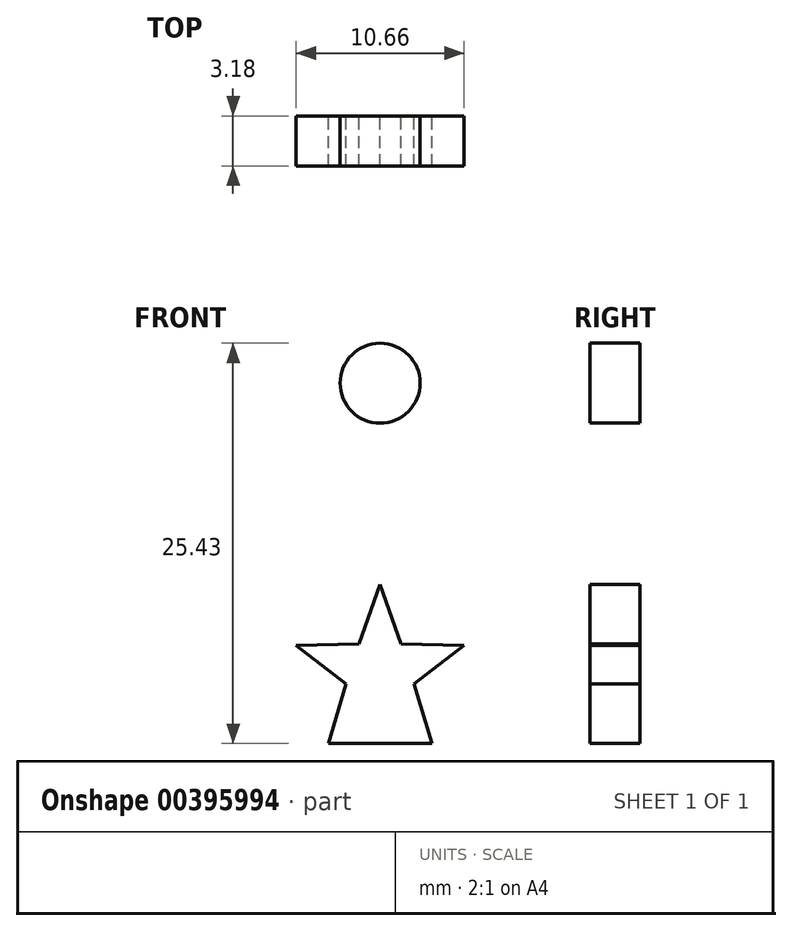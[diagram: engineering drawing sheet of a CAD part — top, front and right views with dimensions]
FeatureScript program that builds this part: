
annotation { "Feature Type Name" : "Feature", "Feature Type Description" : "" }
export const myFeature = defineFeature(function(context is Context, id is Id, definition is map)
    precondition{}
    {
        {
            var Q0;
            Q0=qCreatedBy(makeId("Front.planeOp"),FACE);
            var sketch = newSketch(context, id + "F0", { "sketchPlane" : qUnion([Q0])});
            skLineSegment(sketch, "E0", {"start": v(-0.1, 38.27) * mm, "end": v(-3.28, 38.27) * mm});
            skLineSegment(sketch, "E1", {"start": v(-3.28, 38.27) * mm, "end": v(-2.16, 42.06) * mm});
            skLineSegment(sketch, "E2", {"start": v(-2.16, 42.06) * mm, "end": v(-5.33, 44.5) * mm});
            skLineSegment(sketch, "E3", {"start": v(-5.33, 44.5) * mm, "end": v(-1.33, 44.6) * mm});
            skLineSegment(sketch, "E4", {"start": v(-1.33, 44.6) * mm, "end": v(0, 48.37) * mm});
            skLineSegment(sketch, "E5", {"start": v(0, 48.37) * mm, "end": v(1.33, 44.6) * mm});
            skLineSegment(sketch, "E6", {"start": v(1.33, 44.6) * mm, "end": v(5.33, 44.5) * mm});
            skLineSegment(sketch, "E7", {"start": v(5.33, 44.5) * mm, "end": v(2.16, 42.06) * mm});
            skLineSegment(sketch, "E8", {"start": v(2.16, 42.06) * mm, "end": v(3.28, 38.27) * mm});
            skLineSegment(sketch, "E9", {"start": v(3.28, 38.27) * mm, "end": v(-0.1, 38.27) * mm});
            skLineSegment(sketch, "E10", {"start": v(-31.05, -65.39) * mm, "end": v(-1.59, -65.39) * mm});
            skLineSegment(sketch, "E11", {"start": v(-1.59, -65.39) * mm, "end": v(-1.59, -0.36) * mm});
            skLineSegment(sketch, "E12", {"start": v(-1.59, -0.36) * mm, "end": v(1.59, -0.36) * mm});
            skLineSegment(sketch, "E13", {"start": v(1.59, -0.36) * mm, "end": v(1.59, -65.39) * mm});
            skLineSegment(sketch, "E14", {"start": v(1.59, -65.39) * mm, "end": v(31.05, -65.39) * mm});
            skLineSegment(sketch, "E15", {"start": v(31.05, -65.39) * mm, "end": v(31.05, -57.77) * mm});
            skLineSegment(sketch, "E16", {"start": v(31.05, -57.77) * mm, "end": v(27.9, -54.66) * mm});
            skLineSegment(sketch, "E17", {"start": v(23.62, -52.86) * mm, "end": v(21.6, -52.86) * mm});
            skLineSegment(sketch, "E18", {"start": v(9.72, -41.76) * mm, "end": v(8.89, -31.88) * mm});
            skLineSegment(sketch, "E19", {"start": v(23.02, -32.1) * mm, "end": v(23.54, -32.53) * mm});
            skLineSegment(sketch, "E20", {"start": v(23.54, -32.53) * mm, "end": v(29.79, -39.65) * mm});
            skLineSegment(sketch, "E21", {"start": v(29.79, -39.65) * mm, "end": v(30.65, -38.56) * mm});
            skLineSegment(sketch, "E22", {"start": v(30.65, -38.56) * mm, "end": v(24.6, -31.68) * mm});
            skLineSegment(sketch, "E23", {"start": v(24.6, -31.68) * mm, "end": v(26.15, -31.56) * mm});
            skLineSegment(sketch, "E24", {"start": v(36.9, -31.24) * mm, "end": v(41.54, -31.28) * mm});
            skLineSegment(sketch, "E25", {"start": v(42.55, -31.58) * mm, "end": v(42.82, -31.78) * mm});
            skLineSegment(sketch, "E26", {"start": v(42.82, -31.78) * mm, "end": v(45.54, -34.23) * mm});
            skLineSegment(sketch, "E27", {"start": v(45.54, -34.23) * mm, "end": v(46.28, -33.04) * mm});
            skLineSegment(sketch, "E28", {"start": v(46.28, -33.04) * mm, "end": v(44.43, -31.37) * mm});
            skLineSegment(sketch, "E29", {"start": v(44.43, -31.37) * mm, "end": v(48.37, -31.55) * mm});
            skLineSegment(sketch, "E30", {"start": v(48.37, -31.55) * mm, "end": v(48.44, -30.07) * mm});
            skLineSegment(sketch, "E31", {"start": v(48.44, -30.07) * mm, "end": v(42.79, -29.82) * mm});
            skLineSegment(sketch, "E32", {"start": v(42.79, -29.82) * mm, "end": v(45.23, -26.96) * mm});
            skLineSegment(sketch, "E33", {"start": v(45.23, -26.96) * mm, "end": v(44.36, -25.9) * mm});
            skLineSegment(sketch, "E34", {"start": v(44.36, -25.9) * mm, "end": v(41.7, -29.01) * mm});
            skLineSegment(sketch, "E35", {"start": v(40.75, -29.68) * mm, "end": v(40.18, -29.77) * mm});
            skLineSegment(sketch, "E36", {"start": v(40.18, -29.77) * mm, "end": v(38.93, -29.75) * mm});
            skLineSegment(sketch, "E37", {"start": v(28.15, -29.96) * mm, "end": v(36.05, -22.74) * mm});
            skLineSegment(sketch, "E38", {"start": v(36.05, -22.74) * mm, "end": v(35.3, -21.56) * mm});
            skLineSegment(sketch, "E39", {"start": v(35.3, -21.56) * mm, "end": v(26.43, -29.66) * mm});
            skLineSegment(sketch, "E40", {"start": v(26.08, -29.9) * mm, "end": v(25.34, -30.14) * mm});
            skLineSegment(sketch, "E41", {"start": v(16.62, -30.53) * mm, "end": v(12.38, -30.51) * mm});
            skLineSegment(sketch, "E42", {"start": v(12.38, -30.51) * mm, "end": v(15.43, -26.53) * mm});
            skLineSegment(sketch, "E43", {"start": v(15.43, -26.53) * mm, "end": v(14.51, -25.52) * mm});
            skLineSegment(sketch, "E44", {"start": v(14.51, -25.52) * mm, "end": v(11.37, -29.64) * mm});
            skLineSegment(sketch, "E45", {"start": v(10.48, -30.32) * mm, "end": v(9.87, -30.44) * mm});
            skLineSegment(sketch, "E46", {"start": v(9.87, -30.44) * mm, "end": v(8.76, -30.37) * mm});
            skLineSegment(sketch, "E47", {"start": v(8.76, -30.37) * mm, "end": v(6.95, -8.97) * mm});
            skLineSegment(sketch, "E48", {"start": v(6.95, -8.97) * mm, "end": v(18.25, -9.22) * mm});
            skLineSegment(sketch, "E49", {"start": v(18.25, -9.22) * mm, "end": v(24, -15.05) * mm});
            skLineSegment(sketch, "E50", {"start": v(24, -15.05) * mm, "end": v(24.8, -13.9) * mm});
            skLineSegment(sketch, "E51", {"start": v(24.8, -13.9) * mm, "end": v(20.18, -9.22) * mm});
            skLineSegment(sketch, "E52", {"start": v(20.18, -9.22) * mm, "end": v(31.03, -9.05) * mm});
            skLineSegment(sketch, "E53", {"start": v(32.03, -9.3) * mm, "end": v(32.45, -9.62) * mm});
            skLineSegment(sketch, "E54", {"start": v(32.45, -9.62) * mm, "end": v(34.33, -11.52) * mm});
            skLineSegment(sketch, "E55", {"start": v(34.33, -11.52) * mm, "end": v(35.13, -10.38) * mm});
            skLineSegment(sketch, "E56", {"start": v(35.13, -10.38) * mm, "end": v(33.72, -8.96) * mm});
            skLineSegment(sketch, "E57", {"start": v(33.72, -8.96) * mm, "end": v(36.34, -8.85) * mm});
            skLineSegment(sketch, "E58", {"start": v(36.34, -8.85) * mm, "end": v(36.3, -7.36) * mm});
            skLineSegment(sketch, "E59", {"start": v(36.3, -7.36) * mm, "end": v(32.78, -7.5) * mm});
            skLineSegment(sketch, "E60", {"start": v(32.78, -7.5) * mm, "end": v(34.25, -4.43) * mm});
            skLineSegment(sketch, "E61", {"start": v(34.25, -4.43) * mm, "end": v(33.17, -3.69) * mm});
            skLineSegment(sketch, "E62", {"start": v(33.17, -3.69) * mm, "end": v(31.91, -6.33) * mm});
            skLineSegment(sketch, "E63", {"start": v(15.62, -7.71) * mm, "end": v(12.56, -7.66) * mm});
            skLineSegment(sketch, "E64", {"start": v(12.56, -7.66) * mm, "end": v(21.21, 0.02) * mm});
            skLineSegment(sketch, "E65", {"start": v(21.21, 0.02) * mm, "end": v(20.47, 1.21) * mm});
            skLineSegment(sketch, "E66", {"start": v(20.47, 1.21) * mm, "end": v(11.1, -7.1) * mm});
            skLineSegment(sketch, "E67", {"start": v(9.81, -7.6) * mm, "end": v(6.83, -7.49) * mm});
            skLineSegment(sketch, "E68", {"start": v(6.83, -7.49) * mm, "end": v(5.27, 11) * mm});
            skLineSegment(sketch, "E69", {"start": v(5.27, 11) * mm, "end": v(7.7, 11.24) * mm});
            skLineSegment(sketch, "E70", {"start": v(9.44, 10.36) * mm, "end": v(9.58, 10.14) * mm});
            skLineSegment(sketch, "E71", {"start": v(9.58, 10.14) * mm, "end": v(12.8, 4.4) * mm});
            skLineSegment(sketch, "E72", {"start": v(12.8, 4.4) * mm, "end": v(13.83, 5.22) * mm});
            skLineSegment(sketch, "E73", {"start": v(13.83, 5.22) * mm, "end": v(10.35, 11.43) * mm});
            skLineSegment(sketch, "E74", {"start": v(23.44, 10.8) * mm, "end": v(23.9, 10.3) * mm});
            skLineSegment(sketch, "E75", {"start": v(23.9, 10.3) * mm, "end": v(25.93, 7.4) * mm});
            skLineSegment(sketch, "E76", {"start": v(25.93, 7.4) * mm, "end": v(26.88, 8.36) * mm});
            skLineSegment(sketch, "E77", {"start": v(26.88, 8.36) * mm, "end": v(24.89, 11.22) * mm});
            skLineSegment(sketch, "E78", {"start": v(24.53, 13.68) * mm, "end": v(24.67, 14.03) * mm});
            skLineSegment(sketch, "E79", {"start": v(24.67, 14.03) * mm, "end": v(25.54, 15.93) * mm});
            skLineSegment(sketch, "E80", {"start": v(25.54, 15.93) * mm, "end": v(24.46, 16.65) * mm});
            skLineSegment(sketch, "E81", {"start": v(24.46, 16.65) * mm, "end": v(23.26, 14.07) * mm});
            skLineSegment(sketch, "E82", {"start": v(21.6, 12.8) * mm, "end": v(21.3, 12.79) * mm});
            skLineSegment(sketch, "E83", {"start": v(21.3, 12.79) * mm, "end": v(20.17, 12.87) * mm});
            skLineSegment(sketch, "E84", {"start": v(13.2, 13.03) * mm, "end": v(15.15, 15.75) * mm});
            skLineSegment(sketch, "E85", {"start": v(15.15, 15.75) * mm, "end": v(14.2, 16.72) * mm});
            skLineSegment(sketch, "E86", {"start": v(14.2, 16.72) * mm, "end": v(12.12, 13.8) * mm});
            skLineSegment(sketch, "E87", {"start": v(11.24, 13.08) * mm, "end": v(10.63, 12.94) * mm});
            skLineSegment(sketch, "E88", {"start": v(10.63, 12.94) * mm, "end": v(5.14, 12.49) * mm});
            skLineSegment(sketch, "E89", {"start": v(5.14, 12.49) * mm, "end": v(4.12, 24.6) * mm});
            skLineSegment(sketch, "E90", {"start": v(4.12, 24.6) * mm, "end": v(8.75, 24.04) * mm});
            skLineSegment(sketch, "E91", {"start": v(9.7, 23.68) * mm, "end": v(9.9, 23.51) * mm});
            skLineSegment(sketch, "E92", {"start": v(9.9, 23.51) * mm, "end": v(13.41, 20.18) * mm});
            skLineSegment(sketch, "E93", {"start": v(13.41, 20.18) * mm, "end": v(14.18, 21.35) * mm});
            skLineSegment(sketch, "E94", {"start": v(14.18, 21.35) * mm, "end": v(11.35, 24.04) * mm});
            skLineSegment(sketch, "E95", {"start": v(19.16, 25.44) * mm, "end": v(18.84, 26.88) * mm});
            skLineSegment(sketch, "E96", {"start": v(18.84, 26.88) * mm, "end": v(16.38, 26.2) * mm});
            skLineSegment(sketch, "E97", {"start": v(16.38, 26.2) * mm, "end": v(17.83, 28.73) * mm});
            skLineSegment(sketch, "E98", {"start": v(17.83, 28.73) * mm, "end": v(16.81, 29.58) * mm});
            skLineSegment(sketch, "E99", {"start": v(16.81, 29.58) * mm, "end": v(15.2, 26.8) * mm});
            skLineSegment(sketch, "E100", {"start": v(9.54, 25.56) * mm, "end": v(11.07, 28.68) * mm});
            skLineSegment(sketch, "E101", {"start": v(11.07, 28.68) * mm, "end": v(10, 29.43) * mm});
            skLineSegment(sketch, "E102", {"start": v(10, 29.43) * mm, "end": v(8.77, 26.93) * mm});
            skLineSegment(sketch, "E103", {"start": v(7.07, 25.7) * mm, "end": v(6.76, 25.71) * mm});
            skLineSegment(sketch, "E104", {"start": v(6.76, 25.71) * mm, "end": v(4, 26.16) * mm});
            skLineSegment(sketch, "E105", {"start": v(4, 26.16) * mm, "end": v(3.23, 35.19) * mm});
            skLineSegment(sketch, "E106", {"start": v(3.23, 35.19) * mm, "end": v(7.77, 32.06) * mm});
            skLineSegment(sketch, "E107", {"start": v(7.77, 32.06) * mm, "end": v(5.09, 41.1) * mm});
            skLineSegment(sketch, "E108", {"start": v(5.09, 41.1) * mm, "end": v(12.58, 46.85) * mm});
            skLineSegment(sketch, "E109", {"start": v(12.58, 46.85) * mm, "end": v(3.14, 47.09) * mm});
            skLineSegment(sketch, "E110", {"start": v(3.14, 47.09) * mm, "end": v(0.81, 53.68) * mm});
            skLineSegment(sketch, "E111", {"start": v(0.81, 53.68) * mm, "end": v(0.81, 57) * mm});
            skLineSegment(sketch, "E112", {"start": v(-0.81, 57) * mm, "end": v(-0.81, 53.68) * mm});
            skLineSegment(sketch, "E113", {"start": v(-0.81, 53.68) * mm, "end": v(-3.14, 47.09) * mm});
            skLineSegment(sketch, "E114", {"start": v(-3.14, 47.09) * mm, "end": v(-12.58, 46.85) * mm});
            skLineSegment(sketch, "E115", {"start": v(-12.58, 46.85) * mm, "end": v(-5.09, 41.1) * mm});
            skLineSegment(sketch, "E116", {"start": v(-5.09, 41.1) * mm, "end": v(-7.77, 32.06) * mm});
            skLineSegment(sketch, "E117", {"start": v(-7.77, 32.06) * mm, "end": v(-3.23, 35.19) * mm});
            skLineSegment(sketch, "E118", {"start": v(-3.23, 35.19) * mm, "end": v(-4, 26.16) * mm});
            skLineSegment(sketch, "E119", {"start": v(-4, 26.16) * mm, "end": v(-6.76, 25.71) * mm});
            skLineSegment(sketch, "E120", {"start": v(-6.76, 25.71) * mm, "end": v(-7.07, 25.7) * mm});
            skLineSegment(sketch, "E121", {"start": v(-8.77, 26.93) * mm, "end": v(-10, 29.43) * mm});
            skLineSegment(sketch, "E122", {"start": v(-10, 29.43) * mm, "end": v(-11.07, 28.68) * mm});
            skLineSegment(sketch, "E123", {"start": v(-11.07, 28.68) * mm, "end": v(-9.54, 25.56) * mm});
            skLineSegment(sketch, "E124", {"start": v(-15.2, 26.8) * mm, "end": v(-16.81, 29.58) * mm});
            skLineSegment(sketch, "E125", {"start": v(-16.81, 29.58) * mm, "end": v(-17.83, 28.73) * mm});
            skLineSegment(sketch, "E126", {"start": v(-17.83, 28.73) * mm, "end": v(-16.38, 26.2) * mm});
            skLineSegment(sketch, "E127", {"start": v(-16.38, 26.2) * mm, "end": v(-18.84, 26.88) * mm});
            skLineSegment(sketch, "E128", {"start": v(-18.84, 26.88) * mm, "end": v(-19.16, 25.44) * mm});
            skLineSegment(sketch, "E129", {"start": v(-11.35, 24.04) * mm, "end": v(-14.18, 21.35) * mm});
            skLineSegment(sketch, "E130", {"start": v(-14.18, 21.35) * mm, "end": v(-13.41, 20.18) * mm});
            skLineSegment(sketch, "E131", {"start": v(-13.41, 20.18) * mm, "end": v(-9.9, 23.51) * mm});
            skLineSegment(sketch, "E132", {"start": v(-9.9, 23.51) * mm, "end": v(-9.7, 23.68) * mm});
            skLineSegment(sketch, "E133", {"start": v(-8.75, 24.04) * mm, "end": v(-4.12, 24.6) * mm});
            skLineSegment(sketch, "E134", {"start": v(-4.12, 24.6) * mm, "end": v(-5.14, 12.49) * mm});
            skLineSegment(sketch, "E135", {"start": v(-5.14, 12.49) * mm, "end": v(-10.63, 12.94) * mm});
            skLineSegment(sketch, "E136", {"start": v(-10.63, 12.94) * mm, "end": v(-11.24, 13.08) * mm});
            skLineSegment(sketch, "E137", {"start": v(-12.12, 13.8) * mm, "end": v(-14.2, 16.72) * mm});
            skLineSegment(sketch, "E138", {"start": v(-14.2, 16.72) * mm, "end": v(-15.15, 15.75) * mm});
            skLineSegment(sketch, "E139", {"start": v(-15.15, 15.75) * mm, "end": v(-13.2, 13.03) * mm});
            skLineSegment(sketch, "E140", {"start": v(-20.17, 12.87) * mm, "end": v(-21.3, 12.79) * mm});
            skLineSegment(sketch, "E141", {"start": v(-21.3, 12.79) * mm, "end": v(-21.6, 12.8) * mm});
            skLineSegment(sketch, "E142", {"start": v(-23.26, 14.07) * mm, "end": v(-24.46, 16.65) * mm});
            skLineSegment(sketch, "E143", {"start": v(-24.46, 16.65) * mm, "end": v(-25.54, 15.93) * mm});
            skLineSegment(sketch, "E144", {"start": v(-25.54, 15.93) * mm, "end": v(-24.67, 14.03) * mm});
            skLineSegment(sketch, "E145", {"start": v(-24.67, 14.03) * mm, "end": v(-24.53, 13.68) * mm});
            skLineSegment(sketch, "E146", {"start": v(-24.89, 11.22) * mm, "end": v(-26.88, 8.36) * mm});
            skLineSegment(sketch, "E147", {"start": v(-26.88, 8.36) * mm, "end": v(-25.93, 7.4) * mm});
            skLineSegment(sketch, "E148", {"start": v(-25.93, 7.4) * mm, "end": v(-23.9, 10.3) * mm});
            skLineSegment(sketch, "E149", {"start": v(-23.9, 10.3) * mm, "end": v(-23.44, 10.8) * mm});
            skLineSegment(sketch, "E150", {"start": v(-10.35, 11.43) * mm, "end": v(-13.83, 5.22) * mm});
            skLineSegment(sketch, "E151", {"start": v(-13.83, 5.22) * mm, "end": v(-12.8, 4.4) * mm});
            skLineSegment(sketch, "E152", {"start": v(-12.8, 4.4) * mm, "end": v(-9.58, 10.14) * mm});
            skLineSegment(sketch, "E153", {"start": v(-9.58, 10.14) * mm, "end": v(-9.44, 10.36) * mm});
            skLineSegment(sketch, "E154", {"start": v(-7.7, 11.24) * mm, "end": v(-5.27, 11) * mm});
            skLineSegment(sketch, "E155", {"start": v(-5.27, 11) * mm, "end": v(-6.83, -7.49) * mm});
            skLineSegment(sketch, "E156", {"start": v(-6.83, -7.49) * mm, "end": v(-9.81, -7.6) * mm});
            skLineSegment(sketch, "E157", {"start": v(-11.1, -7.1) * mm, "end": v(-20.47, 1.21) * mm});
            skLineSegment(sketch, "E158", {"start": v(-20.47, 1.21) * mm, "end": v(-21.21, 0.02) * mm});
            skLineSegment(sketch, "E159", {"start": v(-21.21, 0.02) * mm, "end": v(-12.56, -7.66) * mm});
            skLineSegment(sketch, "E160", {"start": v(-12.56, -7.66) * mm, "end": v(-15.62, -7.71) * mm});
            skLineSegment(sketch, "E161", {"start": v(-31.91, -6.33) * mm, "end": v(-33.17, -3.69) * mm});
            skLineSegment(sketch, "E162", {"start": v(-33.17, -3.69) * mm, "end": v(-34.25, -4.43) * mm});
            skLineSegment(sketch, "E163", {"start": v(-34.25, -4.43) * mm, "end": v(-32.78, -7.5) * mm});
            skLineSegment(sketch, "E164", {"start": v(-32.78, -7.5) * mm, "end": v(-36.3, -7.36) * mm});
            skLineSegment(sketch, "E165", {"start": v(-36.3, -7.36) * mm, "end": v(-36.34, -8.85) * mm});
            skLineSegment(sketch, "E166", {"start": v(-36.34, -8.85) * mm, "end": v(-33.72, -8.96) * mm});
            skLineSegment(sketch, "E167", {"start": v(-33.72, -8.96) * mm, "end": v(-35.13, -10.38) * mm});
            skLineSegment(sketch, "E168", {"start": v(-35.13, -10.38) * mm, "end": v(-34.33, -11.52) * mm});
            skLineSegment(sketch, "E169", {"start": v(-34.33, -11.52) * mm, "end": v(-32.45, -9.62) * mm});
            skLineSegment(sketch, "E170", {"start": v(-32.45, -9.62) * mm, "end": v(-32.03, -9.3) * mm});
            skLineSegment(sketch, "E171", {"start": v(-31.03, -9.05) * mm, "end": v(-20.18, -9.22) * mm});
            skLineSegment(sketch, "E172", {"start": v(-20.18, -9.22) * mm, "end": v(-24.8, -13.9) * mm});
            skLineSegment(sketch, "E173", {"start": v(-24.8, -13.9) * mm, "end": v(-24, -15.05) * mm});
            skLineSegment(sketch, "E174", {"start": v(-24, -15.05) * mm, "end": v(-18.25, -9.22) * mm});
            skLineSegment(sketch, "E175", {"start": v(-18.25, -9.22) * mm, "end": v(-6.95, -8.97) * mm});
            skLineSegment(sketch, "E176", {"start": v(-6.95, -8.97) * mm, "end": v(-8.76, -30.37) * mm});
            skLineSegment(sketch, "E177", {"start": v(-8.76, -30.37) * mm, "end": v(-9.87, -30.44) * mm});
            skLineSegment(sketch, "E178", {"start": v(-9.87, -30.44) * mm, "end": v(-10.48, -30.32) * mm});
            skLineSegment(sketch, "E179", {"start": v(-11.37, -29.64) * mm, "end": v(-14.51, -25.52) * mm});
            skLineSegment(sketch, "E180", {"start": v(-14.51, -25.52) * mm, "end": v(-15.43, -26.53) * mm});
            skLineSegment(sketch, "E181", {"start": v(-15.43, -26.53) * mm, "end": v(-12.38, -30.51) * mm});
            skLineSegment(sketch, "E182", {"start": v(-12.38, -30.51) * mm, "end": v(-16.62, -30.53) * mm});
            skLineSegment(sketch, "E183", {"start": v(-25.34, -30.14) * mm, "end": v(-26.08, -29.9) * mm});
            skLineSegment(sketch, "E184", {"start": v(-26.43, -29.66) * mm, "end": v(-35.3, -21.56) * mm});
            skLineSegment(sketch, "E185", {"start": v(-35.3, -21.56) * mm, "end": v(-36.05, -22.74) * mm});
            skLineSegment(sketch, "E186", {"start": v(-36.05, -22.74) * mm, "end": v(-28.15, -29.96) * mm});
            skLineSegment(sketch, "E187", {"start": v(-38.93, -29.75) * mm, "end": v(-40.18, -29.77) * mm});
            skLineSegment(sketch, "E188", {"start": v(-40.18, -29.77) * mm, "end": v(-40.75, -29.68) * mm});
            skLineSegment(sketch, "E189", {"start": v(-41.7, -29.01) * mm, "end": v(-44.36, -25.9) * mm});
            skLineSegment(sketch, "E190", {"start": v(-44.36, -25.9) * mm, "end": v(-45.23, -26.96) * mm});
            skLineSegment(sketch, "E191", {"start": v(-45.23, -26.96) * mm, "end": v(-42.79, -29.82) * mm});
            skLineSegment(sketch, "E192", {"start": v(-42.79, -29.82) * mm, "end": v(-48.44, -30.07) * mm});
            skLineSegment(sketch, "E193", {"start": v(-48.44, -30.07) * mm, "end": v(-48.37, -31.55) * mm});
            skLineSegment(sketch, "E194", {"start": v(-48.37, -31.55) * mm, "end": v(-44.43, -31.37) * mm});
            skLineSegment(sketch, "E195", {"start": v(-44.43, -31.37) * mm, "end": v(-46.28, -33.04) * mm});
            skLineSegment(sketch, "E196", {"start": v(-46.28, -33.04) * mm, "end": v(-45.54, -34.23) * mm});
            skLineSegment(sketch, "E197", {"start": v(-45.54, -34.23) * mm, "end": v(-42.82, -31.78) * mm});
            skLineSegment(sketch, "E198", {"start": v(-42.82, -31.78) * mm, "end": v(-42.55, -31.58) * mm});
            skLineSegment(sketch, "E199", {"start": v(-41.54, -31.28) * mm, "end": v(-36.9, -31.24) * mm});
            skLineSegment(sketch, "E200", {"start": v(-26.15, -31.56) * mm, "end": v(-24.6, -31.68) * mm});
            skLineSegment(sketch, "E201", {"start": v(-24.6, -31.68) * mm, "end": v(-30.65, -38.56) * mm});
            skLineSegment(sketch, "E202", {"start": v(-30.65, -38.56) * mm, "end": v(-29.79, -39.65) * mm});
            skLineSegment(sketch, "E203", {"start": v(-29.79, -39.65) * mm, "end": v(-23.54, -32.53) * mm});
            skLineSegment(sketch, "E204", {"start": v(-23.54, -32.53) * mm, "end": v(-23.02, -32.1) * mm});
            skLineSegment(sketch, "E205", {"start": v(-8.89, -31.88) * mm, "end": v(-9.72, -41.76) * mm});
            skLineSegment(sketch, "E206", {"start": v(-21.6, -52.86) * mm, "end": v(-23.62, -52.86) * mm});
            skLineSegment(sketch, "E207", {"start": v(-27.9, -54.67) * mm, "end": v(-31.05, -57.77) * mm});
            skLineSegment(sketch, "E208", {"start": v(-31.05, -57.77) * mm, "end": v(-31.05, -65.39) * mm});
            skArc(sketch, "E209", {"start": v(-2.54, 61.16) * mm, "mid": v(-1.8, 59.36) * mm, "end": v(0, 58.62) * mm});
            skArc(sketch, "E210", {"start": v(2.54, 61.16) * mm, "mid": v(0, 63.7) * mm, "end": v(-2.54, 61.16) * mm});
            skArc(sketch, "E211", {"start": v(0, 58.62) * mm, "mid": v(1.8, 59.36) * mm, "end": v(2.54, 61.16) * mm});
            skArc(sketch, "E212", {"start": v(27.9, -54.66) * mm, "mid": v(25.94, -53.33) * mm, "end": v(23.62, -52.86) * mm});
            skArc(sketch, "E213", {"start": v(9.72, -41.76) * mm, "mid": v(14.18, -48.9) * mm, "end": v(21.6, -52.86) * mm});
            skArc(sketch, "E214", {"start": v(8.89, -31.88) * mm, "mid": v(11.05, -31.97) * mm, "end": v(13.22, -32.02) * mm});
            skArc(sketch, "E215", {"start": v(13.22, -32.02) * mm, "mid": v(17.62, -32) * mm, "end": v(22, -31.85) * mm});
            skArc(sketch, "E216", {"start": v(23.02, -32.1) * mm, "mid": v(22.53, -31.9) * mm, "end": v(22, -31.85) * mm});
            skArc(sketch, "E217", {"start": v(36.9, -31.24) * mm, "mid": v(31.52, -31.32) * mm, "end": v(26.15, -31.56) * mm});
            skArc(sketch, "E218", {"start": v(42.55, -31.58) * mm, "mid": v(42.07, -31.35) * mm, "end": v(41.54, -31.28) * mm});
            skArc(sketch, "E219", {"start": v(40.75, -29.68) * mm, "mid": v(41.27, -29.41) * mm, "end": v(41.7, -29.01) * mm});
            skArc(sketch, "E220", {"start": v(38.93, -29.75) * mm, "mid": v(33.54, -29.78) * mm, "end": v(28.15, -29.96) * mm});
            skArc(sketch, "E221", {"start": v(26.08, -29.9) * mm, "mid": v(26.26, -29.8) * mm, "end": v(26.43, -29.66) * mm});
            skArc(sketch, "E222", {"start": v(16.62, -30.54) * mm, "mid": v(20.98, -30.41) * mm, "end": v(25.34, -30.14) * mm});
            skArc(sketch, "E223", {"start": v(10.48, -30.32) * mm, "mid": v(10.97, -30.03) * mm, "end": v(11.37, -29.64) * mm});
            skArc(sketch, "E224", {"start": v(32.03, -9.3) * mm, "mid": v(31.55, -9.1) * mm, "end": v(31.03, -9.05) * mm});
            skArc(sketch, "E225", {"start": v(31.15, -7.25) * mm, "mid": v(31.59, -6.84) * mm, "end": v(31.91, -6.33) * mm});
            skArc(sketch, "E226", {"start": v(30.15, -7.59) * mm, "mid": v(30.67, -7.5) * mm, "end": v(31.15, -7.25) * mm});
            skArc(sketch, "E227", {"start": v(15.62, -7.7) * mm, "mid": v(22.89, -7.72) * mm, "end": v(30.15, -7.59) * mm});
            skArc(sketch, "E228", {"start": v(10.7, -7.38) * mm, "mid": v(10.9, -7.25) * mm, "end": v(11.1, -7.1) * mm});
            skArc(sketch, "E229", {"start": v(9.81, -7.6) * mm, "mid": v(10.27, -7.54) * mm, "end": v(10.7, -7.38) * mm});
            skArc(sketch, "E230", {"start": v(8.5, 11.12) * mm, "mid": v(8.1, 11.23) * mm, "end": v(7.7, 11.24) * mm});
            skArc(sketch, "E231", {"start": v(9.44, 10.36) * mm, "mid": v(9.03, 10.81) * mm, "end": v(8.5, 11.12) * mm});
            skArc(sketch, "E232", {"start": v(17.26, 11.52) * mm, "mid": v(13.8, 11.55) * mm, "end": v(10.35, 11.43) * mm});
            skArc(sketch, "E233", {"start": v(22.47, 11.2) * mm, "mid": v(19.87, 11.4) * mm, "end": v(17.26, 11.52) * mm});
            skArc(sketch, "E234", {"start": v(23.44, 10.8) * mm, "mid": v(22.98, 11.07) * mm, "end": v(22.47, 11.2) * mm});
            skArc(sketch, "E235", {"start": v(24.48, 12.2) * mm, "mid": v(24.63, 11.69) * mm, "end": v(24.89, 11.22) * mm});
            skArc(sketch, "E236", {"start": v(24.53, 13.68) * mm, "mid": v(24.4, 12.94) * mm, "end": v(24.48, 12.2) * mm});
            skArc(sketch, "E237", {"start": v(22.7, 13.3) * mm, "mid": v(23.02, 13.65) * mm, "end": v(23.26, 14.07) * mm});
            skArc(sketch, "E238", {"start": v(21.6, 12.79) * mm, "mid": v(22.2, 12.95) * mm, "end": v(22.7, 13.3) * mm});
            skArc(sketch, "E239", {"start": v(20.17, 12.87) * mm, "mid": v(16.69, 13.03) * mm, "end": v(13.2, 13.03) * mm});
            skArc(sketch, "E240", {"start": v(11.24, 13.08) * mm, "mid": v(11.73, 13.38) * mm, "end": v(12.12, 13.8) * mm});
            skArc(sketch, "E241", {"start": v(9.7, 23.68) * mm, "mid": v(9.25, 23.93) * mm, "end": v(8.75, 24.05) * mm});
            skArc(sketch, "E242", {"start": v(11.35, 24.04) * mm, "mid": v(13.21, 24.18) * mm, "end": v(15.07, 24.44) * mm});
            skArc(sketch, "E243", {"start": v(15.07, 24.43) * mm, "mid": v(17.13, 24.87) * mm, "end": v(19.16, 25.44) * mm});
            skArc(sketch, "E244", {"start": v(14.38, 25.96) * mm, "mid": v(14.85, 26.33) * mm, "end": v(15.2, 26.8) * mm});
            skArc(sketch, "E245", {"start": v(13.72, 25.73) * mm, "mid": v(14.06, 25.81) * mm, "end": v(14.38, 25.96) * mm});
            skArc(sketch, "E246", {"start": v(9.54, 25.56) * mm, "mid": v(11.63, 25.57) * mm, "end": v(13.72, 25.73) * mm});
            skArc(sketch, "E247", {"start": v(8.17, 26.17) * mm, "mid": v(8.5, 26.52) * mm, "end": v(8.77, 26.93) * mm});
            skArc(sketch, "E248", {"start": v(7.07, 25.7) * mm, "mid": v(7.66, 25.84) * mm, "end": v(8.17, 26.17) * mm});
            skArc(sketch, "E249", {"start": v(0.81, 57) * mm, "mid": v(3.27, 58.47) * mm, "end": v(4.23, 61.16) * mm});
            skArc(sketch, "E250", {"start": v(4.23, 61.16) * mm, "mid": v(0, 65.39) * mm, "end": v(-4.23, 61.16) * mm});
            skArc(sketch, "E251", {"start": v(-4.23, 61.16) * mm, "mid": v(-3.27, 58.47) * mm, "end": v(-0.81, 57) * mm});
            skArc(sketch, "E252", {"start": v(-8.17, 26.17) * mm, "mid": v(-7.66, 25.84) * mm, "end": v(-7.07, 25.7) * mm});
            skArc(sketch, "E253", {"start": v(-8.77, 26.93) * mm, "mid": v(-8.5, 26.52) * mm, "end": v(-8.17, 26.17) * mm});
            skArc(sketch, "E254", {"start": v(-13.72, 25.73) * mm, "mid": v(-11.63, 25.57) * mm, "end": v(-9.54, 25.56) * mm});
            skArc(sketch, "E255", {"start": v(-14.38, 25.96) * mm, "mid": v(-14.06, 25.81) * mm, "end": v(-13.72, 25.73) * mm});
            skArc(sketch, "E256", {"start": v(-15.2, 26.8) * mm, "mid": v(-14.85, 26.33) * mm, "end": v(-14.38, 25.96) * mm});
            skArc(sketch, "E257", {"start": v(-19.16, 25.44) * mm, "mid": v(-17.13, 24.87) * mm, "end": v(-15.07, 24.43) * mm});
            skArc(sketch, "E258", {"start": v(-15.07, 24.44) * mm, "mid": v(-13.21, 24.18) * mm, "end": v(-11.35, 24.04) * mm});
            skArc(sketch, "E259", {"start": v(-8.75, 24.05) * mm, "mid": v(-9.25, 23.93) * mm, "end": v(-9.7, 23.68) * mm});
            skArc(sketch, "E260", {"start": v(-12.12, 13.8) * mm, "mid": v(-11.73, 13.39) * mm, "end": v(-11.24, 13.08) * mm});
            skArc(sketch, "E261", {"start": v(-13.2, 13.03) * mm, "mid": v(-16.69, 13.03) * mm, "end": v(-20.17, 12.87) * mm});
            skArc(sketch, "E262", {"start": v(-22.7, 13.3) * mm, "mid": v(-22.2, 12.95) * mm, "end": v(-21.6, 12.79) * mm});
            skArc(sketch, "E263", {"start": v(-23.26, 14.07) * mm, "mid": v(-23.02, 13.65) * mm, "end": v(-22.7, 13.3) * mm});
            skArc(sketch, "E264", {"start": v(-24.48, 12.2) * mm, "mid": v(-24.4, 12.94) * mm, "end": v(-24.53, 13.68) * mm});
            skArc(sketch, "E265", {"start": v(-24.89, 11.22) * mm, "mid": v(-24.63, 11.69) * mm, "end": v(-24.48, 12.2) * mm});
            skArc(sketch, "E266", {"start": v(-22.47, 11.2) * mm, "mid": v(-22.98, 11.07) * mm, "end": v(-23.44, 10.8) * mm});
            skArc(sketch, "E267", {"start": v(-17.26, 11.52) * mm, "mid": v(-19.87, 11.4) * mm, "end": v(-22.47, 11.2) * mm});
            skArc(sketch, "E268", {"start": v(-10.35, 11.43) * mm, "mid": v(-13.8, 11.55) * mm, "end": v(-17.26, 11.52) * mm});
            skArc(sketch, "E269", {"start": v(-8.5, 11.12) * mm, "mid": v(-9.03, 10.81) * mm, "end": v(-9.44, 10.36) * mm});
            skArc(sketch, "E270", {"start": v(-7.7, 11.24) * mm, "mid": v(-8.1, 11.23) * mm, "end": v(-8.5, 11.12) * mm});
            skArc(sketch, "E271", {"start": v(-10.7, -7.38) * mm, "mid": v(-10.27, -7.54) * mm, "end": v(-9.81, -7.6) * mm});
            skArc(sketch, "E272", {"start": v(-11.1, -7.1) * mm, "mid": v(-10.9, -7.25) * mm, "end": v(-10.7, -7.38) * mm});
            skArc(sketch, "E273", {"start": v(-30.15, -7.59) * mm, "mid": v(-22.89, -7.72) * mm, "end": v(-15.62, -7.7) * mm});
            skArc(sketch, "E274", {"start": v(-31.14, -7.25) * mm, "mid": v(-30.67, -7.5) * mm, "end": v(-30.15, -7.59) * mm});
            skArc(sketch, "E275", {"start": v(-31.91, -6.33) * mm, "mid": v(-31.59, -6.84) * mm, "end": v(-31.15, -7.25) * mm});
            skArc(sketch, "E276", {"start": v(-31.03, -9.06) * mm, "mid": v(-31.55, -9.1) * mm, "end": v(-32.03, -9.3) * mm});
            skArc(sketch, "E277", {"start": v(-11.37, -29.64) * mm, "mid": v(-10.97, -30.03) * mm, "end": v(-10.48, -30.32) * mm});
            skArc(sketch, "E278", {"start": v(-25.34, -30.13) * mm, "mid": v(-20.98, -30.4) * mm, "end": v(-16.62, -30.53) * mm});
            skArc(sketch, "E279", {"start": v(-26.43, -29.66) * mm, "mid": v(-26.26, -29.8) * mm, "end": v(-26.08, -29.9) * mm});
            skArc(sketch, "E280", {"start": v(-28.15, -29.96) * mm, "mid": v(-33.54, -29.78) * mm, "end": v(-38.93, -29.75) * mm});
            skArc(sketch, "E281", {"start": v(-41.7, -29.01) * mm, "mid": v(-41.27, -29.42) * mm, "end": v(-40.75, -29.68) * mm});
            skArc(sketch, "E282", {"start": v(-41.54, -31.28) * mm, "mid": v(-42.07, -31.36) * mm, "end": v(-42.55, -31.58) * mm});
            skArc(sketch, "E283", {"start": v(-26.15, -31.56) * mm, "mid": v(-31.52, -31.32) * mm, "end": v(-36.9, -31.24) * mm});
            skArc(sketch, "E284", {"start": v(-22, -31.85) * mm, "mid": v(-22.53, -31.9) * mm, "end": v(-23.02, -32.1) * mm});
            skArc(sketch, "E285", {"start": v(-22, -31.85) * mm, "mid": v(-17.62, -32) * mm, "end": v(-13.22, -32.02) * mm});
            skArc(sketch, "E286", {"start": v(-13.22, -32.02) * mm, "mid": v(-11.05, -31.97) * mm, "end": v(-8.89, -31.88) * mm});
            skArc(sketch, "E287", {"start": v(-21.6, -52.86) * mm, "mid": v(-14.18, -48.9) * mm, "end": v(-9.72, -41.76) * mm});
            skArc(sketch, "E288", {"start": v(-23.62, -52.86) * mm, "mid": v(-25.94, -53.33) * mm, "end": v(-27.9, -54.67) * mm});
            skSolve(sketch);
        }
        {
            var Q0;
            Q0 = qSketchRegion(id + "F0", true);
            extrude(context, id + "F1", {"entities" : qUnion([Q0]), "endBound" : BoundingType.SYMMETRIC, "depth" : 3.17 * mm});
        }
    });
